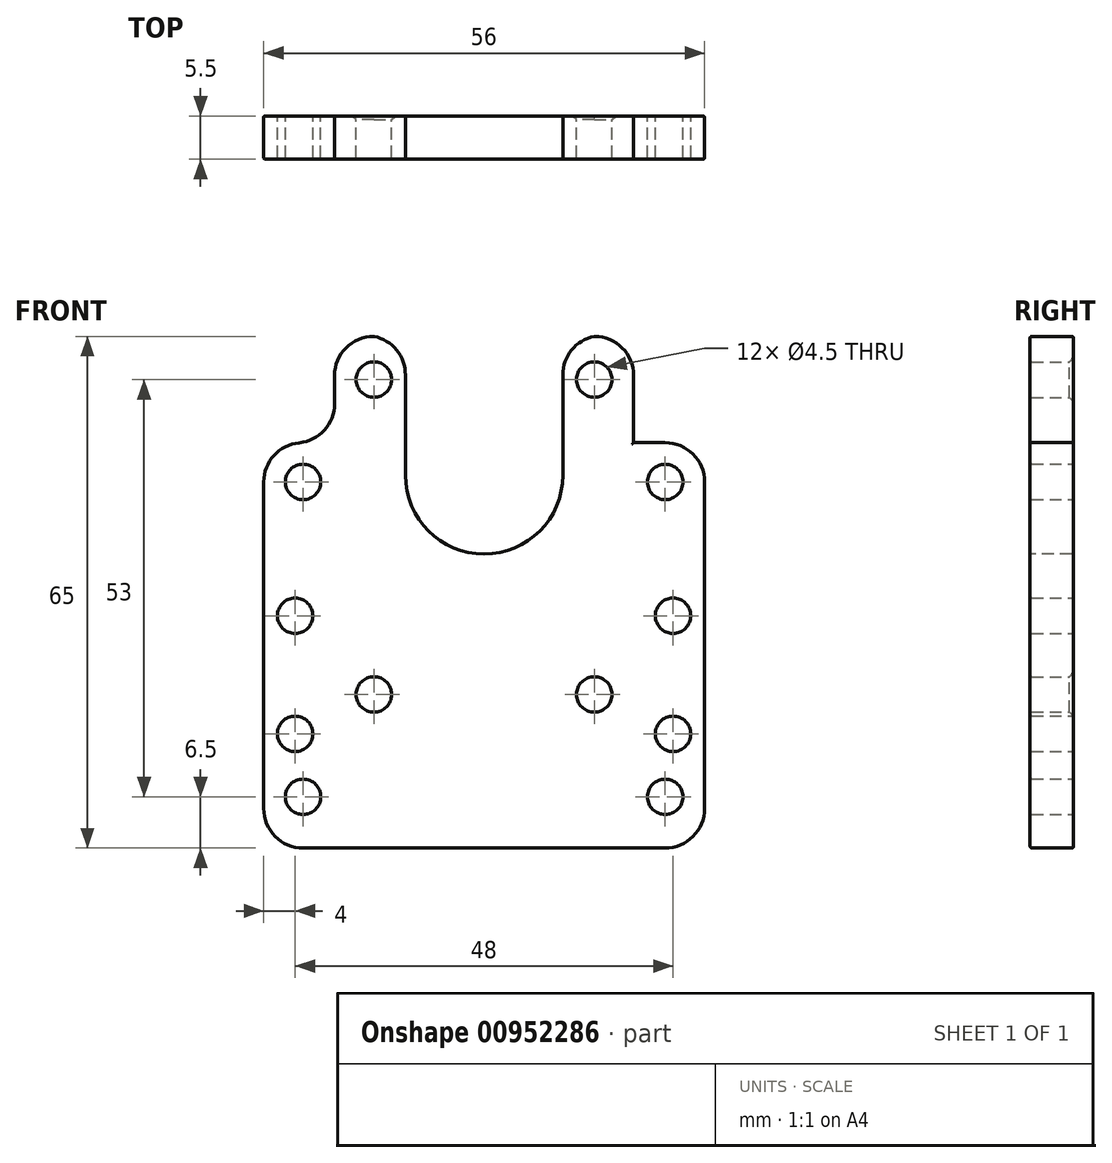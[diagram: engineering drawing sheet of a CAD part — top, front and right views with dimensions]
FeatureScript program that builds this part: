
annotation { "Feature Type Name" : "Feature", "Feature Type Description" : "" }
export const myFeature = defineFeature(function(context is Context, id is Id, definition is map)
    precondition{}
    {
        {
            var Q0;
            Q0=qCreatedBy(makeId("Front.planeOp"),FACE);
            cPlane(context, id + "F0", {"entities" : qUnion([Q0]), "cplaneType" : CPlaneType.OFFSET, "offset" : 13 * mm, "width" : 150 * mm, "height" : 150 * mm});
        }
        {
            var Q0;
            Q0=qCreatedBy(id+"F0.planeOp",FACE);
            var sketch = newSketch(context, id + "F1", { "sketchPlane" : qUnion([Q0])});
            skLineSegment(sketch, "E0.bottom", {"start": v(12, 56.5) * mm, "end": v(50, 56.5) * mm});
            skLineSegment(sketch, "E0.left", {"start": v(12, 56.5) * mm, "end": v(12, -8.5) * mm});
            skLineSegment(sketch, "E0.right", {"start": v(50, 56.5) * mm, "end": v(50, -8.5) * mm});
            skLineSegment(sketch, "E1", {"start": v(31, 77.62) * mm, "end": v(31, -1.76) * mm, "construction": true});
            skLineSegment(sketch, "E2", {"start": v(-19.07, 31) * mm, "end": v(89.66, 31) * mm, "construction": true});
            skCircle(sketch, "E3", {"center": v(45, 51) * mm, "radius": 2.25 * mm});
            skCircle(sketch, "E4", {"center": v(45, 11) * mm, "radius": 2.25 * mm});
            skCircle(sketch, "E5", {"center": v(17, 11) * mm, "radius": 2.25 * mm});
            skCircle(sketch, "E6", {"center": v(17, 51) * mm, "radius": 2.25 * mm});
            skCircle(sketch, "E7", {"center": v(17, 11) * mm, "radius": 3.5 * mm, "construction": true});
            skCircle(sketch, "E8", {"center": v(45, 11) * mm, "radius": 3.5 * mm, "construction": true});
            skCircle(sketch, "E9", {"center": v(17, 51) * mm, "radius": 3.5 * mm, "construction": true});
            skCircle(sketch, "E10", {"center": v(45, 51) * mm, "radius": 3.5 * mm, "construction": true});
            skLineSegment(sketch, "E11", {"start": v(37.5, 20.8) * mm, "end": v(37.5, 18.3) * mm, "construction": true});
            skCircle(sketch, "E12", {"center": v(24.5, 19.55) * mm, "radius": 1.25 * mm});
            skLineSegment(sketch, "E13", {"start": v(38.75, 19.55) * mm, "end": v(36.25, 19.55) * mm, "construction": true});
            skCircle(sketch, "E14", {"center": v(37.5, 19.55) * mm, "radius": 1.25 * mm});
            skCircle(sketch, "E15", {"center": v(7, 6) * mm, "radius": 2.25 * mm});
            skCircle(sketch, "E16.MirrorC", {"center": v(7, 21) * mm, "radius": 2.25 * mm});
            skLineSegment(sketch, "E17.top", {"start": v(50, -8.5) * mm, "end": v(12, -8.5) * mm});
            skArc(sketch, "E18.MirrorCS", {"start": v(8, -8.5) * mm, "mid": v(4.46, -7.04) * mm, "end": v(3, -3.5) * mm});
            skLineSegment(sketch, "E19", {"start": v(8, -8.5) * mm, "end": v(12, -8.5) * mm});
            skPoint(sketch, "E20.MirrorCS.center.orphan", {"position": v(7, 31) * mm});
            skLineSegment(sketch, "E21", {"start": v(3, 38) * mm, "end": v(3, -3.5) * mm});
            skCircle(sketch, "E22", {"center": v(8, -2) * mm, "radius": 2.25 * mm});
            skCircle(sketch, "E23", {"center": v(8, 38) * mm, "radius": 2.25 * mm});
            skArc(sketch, "E24", {"start": v(8, 43) * mm, "mid": v(4.46, 41.54) * mm, "end": v(3, 38) * mm});
            skLineSegment(sketch, "E25", {"start": v(8, 43) * mm, "end": v(12, 43) * mm});
            skSolve(sketch);
        }
        {
            var Q0;
            {var subQ1=sQuery(id+"F1.wireOp",EDGE,"E0.bottom");Q0=makeQuery(id+"F1.imprint","IMPRINT",FACE,{"disambiguationData":[TD([[makeQuery(id+"F1.imprint","IMPRINT",EDGE,{"derivedFrom":subQ1}),-1.0]])]});}
            var Q1;
            {var subQ0=sQuery(id+"F1.wireOp",EDGE,"4c5f126c-7228-4284-9c72-7ca8e39765180.MirrorCS");Q1=makeQuery(id+"F1.imprint","IMPRINT",FACE,{"disambiguationData":[TD([[makeQuery(id+"F1.imprint","IMPRINT",EDGE,{"derivedFrom":subQ0}),1.0]])]});}
            var Q2;
            {var subQ0=sQuery(id+"F1.wireOp",EDGE,"bd2f8090-7cf7-4306-adcd-41070bc121290.MirrorCS");Q2=makeQuery(id+"F1.imprint","IMPRINT",FACE,{"disambiguationData":[TD([[makeQuery(id+"F1.imprint","IMPRINT",EDGE,{"derivedFrom":subQ0}),1.0]])]});}
            var Q3;
            {var subQ0=sQuery(id+"F1.wireOp",EDGE,"4c5f126c-7228-4284-9c72-7ca8e39765180.MirrorCS");Q3=makeQuery(id+"F1.imprint","IMPRINT",FACE,{"disambiguationData":[TD([[makeQuery(id+"F1.imprint","IMPRINT",EDGE,{"derivedFrom":subQ0}),-1.0]])]});}
            var Q4;
            {var subQ0=sQuery(id+"F1.wireOp",EDGE,"E20.MirrorCS");var subQ1=makeQuery(id+"F1.imprint","INTERSECT",VERTEX,{"derivedFrom":[sQuery(id+"F1.wireOp",EDGE,"4c5f126c-7228-4284-9c72-7ca8e39765180.MirrorCS"),subQ0]});Q4=makeQuery(id+"F1.imprint","IMPRINT",FACE,{"disambiguationData":[TD([[makeQuery(id+"F1.imprint","IMPRINT",EDGE,{"disambiguationData":[TD([[subQ1,1.0]])],"derivedFrom":subQ0}),-1.0]])]});}
            var Q5;
            {var subQ0=sQuery(id+"F1.wireOp",EDGE,"28a49bcd-20f1-45de-a4e1-923c5660a67d0.MirrorCS");Q5=makeQuery(id+"F1.imprint","IMPRINT",FACE,{"disambiguationData":[TD([[makeQuery(id+"F1.imprint","IMPRINT",EDGE,{"derivedFrom":subQ0}),-1.0]])]});}
            var Q6;
            {var subQ0=sQuery(id+"F1.wireOp",EDGE,"14a62f3c-94eb-4a37-8f73-e40623ff29c70.MirrorCS");var subQ3=sQuery(id+"F1.wireOp",EDGE,"E20.MirrorCS");var subQ5=makeQuery(id+"F1.imprint","INTERSECT",VERTEX,{"disambiguationData":[OD(1.0)],"derivedFrom":[subQ3,subQ0]});Q6=makeQuery(id+"F1.imprint","IMPRINT",FACE,{"disambiguationData":[TD([[makeQuery(id+"F1.imprint","IMPRINT",EDGE,{"disambiguationData":[TD([[subQ5,1.0]])],"derivedFrom":subQ3}),1.0]])]});}
            var Q7;
            {var subQ0=sQuery(id+"F1.wireOp",EDGE,"c9f7c960-82de-4ad7-af7f-67adeb7fb3330.MirrorCS");Q7=makeQuery(id+"F1.imprint","IMPRINT",FACE,{"disambiguationData":[TD([[makeQuery(id+"F1.imprint","IMPRINT",EDGE,{"derivedFrom":subQ0}),1.0]])]});}
            var Q8;
            {var subQ3=sQuery(id+"F1.wireOp",EDGE,"540323be-f487-4806-8fb1-764a1782e5200.MirrorCS");Q8=makeQuery(id+"F1.imprint","IMPRINT",FACE,{"disambiguationData":[TD([[makeQuery(id+"F1.imprint","IMPRINT",EDGE,{"derivedFrom":subQ3}),-1.0]])]});}
            var Q9;
            {var subQ0=sQuery(id+"F1.wireOp",EDGE,"E20.MirrorCS");var subQ3=sQuery(id+"F1.wireOp",EDGE,"81622e4d-bb80-4ace-9f8c-d33d0fcbef830.MirrorCS");var subQ5=makeQuery(id+"F1.imprint","INTERSECT",VERTEX,{"disambiguationData":[OD(1.0)],"derivedFrom":[subQ0,subQ3]});Q9=makeQuery(id+"F1.imprint","IMPRINT",FACE,{"disambiguationData":[TD([[makeQuery(id+"F1.imprint","IMPRINT",EDGE,{"disambiguationData":[TD([[subQ5,-1.0]])],"derivedFrom":subQ0}),1.0]])]});}
            var Q10;
            {var subQ0=sQuery(id+"F1.wireOp",EDGE,"E20.MirrorCS");var subQ1=makeQuery(id+"F1.imprint","INTERSECT",VERTEX,{"derivedFrom":[subQ0,sQuery(id+"F1.wireOp",EDGE,"c9f7c960-82de-4ad7-af7f-67adeb7fb3330.MirrorCS")]});Q10=makeQuery(id+"F1.imprint","IMPRINT",FACE,{"disambiguationData":[TD([[makeQuery(id+"F1.imprint","IMPRINT",EDGE,{"disambiguationData":[TD([[subQ1,1.0]])],"derivedFrom":subQ0}),-1.0]])]});}
            var Q11;
            {var subQ0=sQuery(id+"F1.wireOp",EDGE,"c9f7c960-82de-4ad7-af7f-67adeb7fb3330.MirrorCS");Q11=makeQuery(id+"F1.imprint","IMPRINT",FACE,{"disambiguationData":[TD([[makeQuery(id+"F1.imprint","IMPRINT",EDGE,{"derivedFrom":subQ0}),-1.0]])]});}
            var Q12;
            {var subQ0=sQuery(id+"F1.wireOp",EDGE,"2b5f1761-41bf-4c5f-a052-8d6cd96bd7f80.MirrorCS");Q12=makeQuery(id+"F1.imprint","IMPRINT",FACE,{"disambiguationData":[TD([[makeQuery(id+"F1.imprint","IMPRINT",EDGE,{"derivedFrom":subQ0}),1.0]])]});}
            var Q13;
            Q13=makeQuery(id+"F1.imprint","IMPRINT",FACE,{"disambiguationData":[TD([[makeQuery(id+"F1.imprint","IMPRINT",EDGE,{"derivedFrom":sQuery(id+"F1.wireOp",EDGE,"044e4ed2-c594-4609-a6b1-d96679fc13440.MirrorC")}),1.0]])]});
            var Q14;
            {var subQ0=sQuery(id+"F1.wireOp",EDGE,"YvGRB0oB-o1B7-2Eru-9MpJ-MU3ItPoMbeSP");var subQ1=sQuery(id+"F1.wireOp",EDGE,"E20.MirrorCS");var subQ2=makeQuery(id+"F1.imprint","INTERSECT",VERTEX,{"derivedFrom":[subQ1,subQ0]});Q14=makeQuery(id+"F1.imprint","IMPRINT",FACE,{"disambiguationData":[TD([[makeQuery(id+"F1.imprint","IMPRINT",EDGE,{"disambiguationData":[TD([[subQ2,-1.0]])],"derivedFrom":subQ1}),1.0]])]});}
            var Q15;
            {var subQ0=sQuery(id+"F1.wireOp",EDGE,"YvGRB0oB-o1B7-2Eru-9MpJ-MU3ItPoMbeSP");var subQ1=sQuery(id+"F1.wireOp",EDGE,"E20.MirrorCS");var subQ2=makeQuery(id+"F1.imprint","INTERSECT",VERTEX,{"derivedFrom":[subQ1,subQ0]});Q15=makeQuery(id+"F1.imprint","IMPRINT",FACE,{"disambiguationData":[TD([[makeQuery(id+"F1.imprint","IMPRINT",EDGE,{"disambiguationData":[TD([[subQ2,1.0]])],"derivedFrom":subQ1}),1.0]])]});}
            var Q16;
            Q16=makeQuery(id+"F1.imprint","IMPRINT",FACE,{"disambiguationData":[TD([[makeQuery(id+"F1.imprint","IMPRINT",EDGE,{"derivedFrom":sQuery(id+"F1.wireOp",EDGE,"044e4ed2-c594-4609-a6b1-d96679fc13440.MirrorC")}),-1.0]])]});
            var Q17;
            {var subQ0=sQuery(id+"F1.wireOp",EDGE,"14a62f3c-94eb-4a37-8f73-e40623ff29c70.MirrorCS");var subQ3=sQuery(id+"F1.wireOp",EDGE,"E20.MirrorCS");var subQ5=makeQuery(id+"F1.imprint","INTERSECT",VERTEX,{"disambiguationData":[OD(0.0)],"derivedFrom":[subQ3,subQ0]});Q17=makeQuery(id+"F1.imprint","IMPRINT",FACE,{"disambiguationData":[TD([[makeQuery(id+"F1.imprint","IMPRINT",EDGE,{"disambiguationData":[TD([[subQ5,1.0]])],"derivedFrom":subQ3}),1.0]])]});}
            var Q18;
            {var subQ1=sQuery(id+"F1.wireOp",EDGE,"81NgzbPt-EB3h-myks-LzxL-Qv06gequt6FA");Q18=makeQuery(id+"F1.imprint","IMPRINT",FACE,{"disambiguationData":[TD([[makeQuery(id+"F1.imprint","IMPRINT",EDGE,{"derivedFrom":subQ1}),1.0]])]});}
            var Q19;
            Q19=makeQuery(id+"F1.imprint","IMPRINT",FACE,{"disambiguationData":[TD([[makeQuery(id+"F1.imprint","IMPRINT",EDGE,{"derivedFrom":sQuery(id+"F1.wireOp",EDGE,"E15")}),-1.0]])]});
            var Q20;
            {var subQ3=sQuery(id+"F1.wireOp",EDGE,"81NgzbPt-EB3h-myks-LzxL-Qv06gequt6FA");Q20=makeQuery(id+"F1.imprint","IMPRINT",FACE,{"disambiguationData":[TD([[makeQuery(id+"F1.imprint","IMPRINT",EDGE,{"derivedFrom":subQ3}),-1.0]])]});}
            var Q21;
            {var subQ3=sQuery(id+"F1.wireOp",EDGE,"ZM5MgDSH-fxbz-2lXx-OnJi-46qlj0q2sVRy");Q21=makeQuery(id+"F1.imprint","IMPRINT",FACE,{"disambiguationData":[TD([[makeQuery(id+"F1.imprint","IMPRINT",EDGE,{"derivedFrom":subQ3}),1.0]])]});}
            var Q22;
            {var subQ0=sQuery(id+"F1.wireOp",EDGE,"ZM5MgDSH-fxbz-2lXx-OnJi-46qlj0q2sVRy");Q22=makeQuery(id+"F1.imprint","IMPRINT",FACE,{"disambiguationData":[TD([[makeQuery(id+"F1.imprint","IMPRINT",EDGE,{"derivedFrom":subQ0}),-1.0]])]});}
            var Q23;
            Q23=makeQuery(id+"F1.imprint","IMPRINT",FACE,{"disambiguationData":[TD([[makeQuery(id+"F1.imprint","IMPRINT",EDGE,{"derivedFrom":sQuery(id+"F1.wireOp",EDGE,"0455397c-a53a-48e8-8fdc-598eec077b450.MirrorC")}),1.0]])]});
            var Q24;
            {var subQ1=sQuery(id+"F1.wireOp",EDGE,"E17.bottom");Q24=makeQuery(id+"F1.imprint","IMPRINT",FACE,{"disambiguationData":[TD([[makeQuery(id+"F1.imprint","IMPRINT",EDGE,{"derivedFrom":subQ1}),1.0]])]});}
            var Q25;
            {var subQ0=sQuery(id+"F1.wireOp",EDGE,"E19");Q25=makeQuery(id+"F1.imprint","IMPRINT",FACE,{"disambiguationData":[TD([[makeQuery(id+"F1.imprint","IMPRINT",EDGE,{"derivedFrom":subQ0}),1.0]])]});}
            var Q26;
            {var subQ5=sQuery(id+"F1.wireOp",EDGE,"ASwXeTtA-wzrH-nalq-PQ0O-iZlBfhMEutyM.bottom");Q26=makeQuery(id+"F1.imprint","IMPRINT",FACE,{"disambiguationData":[TD([[makeQuery(id+"F1.imprint","IMPRINT",EDGE,{"derivedFrom":subQ5}),-1.0]])]});}
            var Q27;
            {var subQ0=sQuery(id+"F1.wireOp",EDGE,"E18.MirrorCS");var subQ1=sQuery(id+"F1.wireOp",EDGE,"E17.right");var subQ2=makeQuery(id+"F1.imprint","INTERSECT",VERTEX,{"disambiguationData":[OD(0.0)],"derivedFrom":[subQ1,subQ0]});Q27=makeQuery(id+"F1.imprint","IMPRINT",FACE,{"disambiguationData":[TD([[makeQuery(id+"F1.imprint","IMPRINT",EDGE,{"disambiguationData":[TD([[subQ2,1.0]])],"derivedFrom":subQ1}),1.0]])]});}
            var Q28;
            Q28=makeQuery(id+"F1.imprint","IMPRINT",FACE,{"disambiguationData":[TD([[makeQuery(id+"F1.imprint","IMPRINT",EDGE,{"derivedFrom":sQuery(id+"F1.wireOp",EDGE,"E12")}),1.0]])]});
            var Q29;
            Q29=makeQuery(id+"F1.imprint","IMPRINT",FACE,{"disambiguationData":[TD([[makeQuery(id+"F1.imprint","IMPRINT",EDGE,{"derivedFrom":sQuery(id+"F1.wireOp",EDGE,"E14")}),1.0]])]});
            extrude(context, id + "F2", {"entities" : qUnion([Q0, Q1, Q2, Q3, Q4, Q5, Q6, Q7, Q8, Q9, Q10, Q11, Q12, Q13, Q14, Q15, Q16, Q17, Q18, Q19, Q20, Q21, Q22, Q23, Q24, Q25, Q26, Q27, Q28, Q29]), "depth" : (4.5 + 1) * mm, "offsetDistance" : 25 * mm});
        }
        {
            var Q0;
            Q0=qCreatedBy(makeId("Front.planeOp"),FACE);
            cPlane(context, id + "F3", {"entities" : qUnion([Q0]), "cplaneType" : CPlaneType.OFFSET, "offset" : 13 * mm, "width" : 150 * mm, "height" : 150 * mm});
        }
        {
            var Q0;
            Q0=qCreatedBy(id+"F3.planeOp",FACE);
            var sketch = newSketch(context, id + "F4", { "sketchPlane" : qUnion([Q0])});
            skLineSegment(sketch, "E26.bottom", {"start": v(26, 70.22) * mm, "end": v(36, 70.22) * mm});
            skLineSegment(sketch, "E26.top", {"start": v(26, 32.5) * mm, "end": v(36, 32.5) * mm});
            skLineSegment(sketch, "E26.left", {"start": v(26, 70.22) * mm, "end": v(26, 32.5) * mm});
            skLineSegment(sketch, "E26.right", {"start": v(36, 70.22) * mm, "end": v(36, 32.5) * mm});
            skLineSegment(sketch, "E27", {"start": v(31, 83.23) * mm, "end": v(31, -17.57) * mm, "construction": true});
            skSolve(sketch);
        }
        {
            var Q0;
            Q0 = qSketchRegion(id + "F4", true);
            extrude(context, id + "F5", {"entities" : qUnion([Q0]), "operationType" : NewBodyOperationType.REMOVE, "endBound" : BoundingType.THROUGH_ALL, "oppositeDirection" : true, "depth" : 25 * mm, "offsetDistance" : 25 * mm});
        }
        {
            var Q0;
            Q0=qCreatedBy(makeId("Front.planeOp"),FACE);
            var Q1;
            Q1 = qBodyType(qCreatedBy(id + "F7" ,EDGE), BodyType.WIRE);
            cPlane(context, id + "F6", {"entities" : qUnion([Q0, Q1]), "cplaneType" : CPlaneType.OFFSET, "offset" : 13 * mm, "width" : 150 * mm, "height" : 150 * mm});
        }
        {
            var Q0;
            Q0=qCreatedBy(id+"F6.planeOp",FACE);
            var sketch = newSketch(context, id + "F7", { "sketchPlane" : qUnion([Q0])});
            skCircle(sketch, "E28", {"center": v(17, 21) * mm, "radius": 2.25 * mm});
            skCircle(sketch, "E29", {"center": v(45, 21) * mm, "radius": 2.25 * mm});
            skSolve(sketch);
        }
        {
            var Q0;
            Q0 = qSketchRegion(id + "F7", true);
            extrude(context, id + "F8", {"entities" : qUnion([Q0]), "operationType" : NewBodyOperationType.REMOVE, "endBound" : BoundingType.THROUGH_ALL, "oppositeDirection" : true, "depth" : 25 * mm, "offsetDistance" : 25 * mm});
        }
        {
            var Q0;
            Q0=qCreatedBy(makeId("Front.planeOp"),FACE);
            cPlane(context, id + "F9", {"entities" : qUnion([Q0]), "cplaneType" : CPlaneType.OFFSET, "offset" : 10 * mm, "width" : 150 * mm, "height" : 150 * mm});
        }
        {
            var Q0;
            Q0=qCreatedBy(id+"F9.planeOp",FACE);
            var sketch = newSketch(context, id + "F10", { "sketchPlane" : qUnion([Q0])});
            skArc(sketch, "E30", {"start": v(17, 16) * mm, "mid": v(22, 21) * mm, "end": v(17, 26) * mm});
            skArc(sketch, "E31", {"start": v(45, 26) * mm, "mid": v(40, 21) * mm, "end": v(45, 16) * mm});
            skLineSegment(sketch, "E32", {"start": v(17, 26) * mm, "end": v(3.21, 26) * mm});
            skLineSegment(sketch, "E33", {"start": v(3.21, 26) * mm, "end": v(3.21, 16) * mm});
            skLineSegment(sketch, "E34", {"start": v(3.21, 16) * mm, "end": v(17, 16) * mm});
            skLineSegment(sketch, "E35", {"start": v(45, 26) * mm, "end": v(58.79, 26) * mm});
            skLineSegment(sketch, "E36", {"start": v(58.79, 26) * mm, "end": v(58.79, 16) * mm});
            skLineSegment(sketch, "E37", {"start": v(58.79, 16) * mm, "end": v(45, 16) * mm});
            skSolve(sketch);
        }
        {
            var Q0;
            Q0 = qSketchRegion(id + "F10", true);
            var Q1;
            Q1 = qSketchRegion(id + "F10", true);
            extrude(context, id + "F11", {"entities" : qUnion([Q0, Q1]), "operationType" : NewBodyOperationType.REMOVE, "endBound" : BoundingType.THROUGH_ALL, "oppositeDirection" : true, "depth" : 25 * mm, "offsetDistance" : 25 * mm});
        }
        {
            var Q0;
            Q0=makeQuery(id+"F2.opExtrude","CAP_FACE",FACE,{"disambiguationData":[OSD([sQuery(id+"F1.wireOp",EDGE,"E0.bottom"),sQuery(id+"F1.wireOp",EDGE,"E0.top"),sQuery(id+"F1.wireOp",EDGE,"E0.left"),sQuery(id+"F1.wireOp",EDGE,"E0.right"),sQuery(id+"F1.wireOp",EDGE,"E3"),sQuery(id+"F1.wireOp",EDGE,"E4"),sQuery(id+"F1.wireOp",EDGE,"E5"),sQuery(id+"F1.wireOp",EDGE,"E6"),sQuery(id+"F1.wireOp",EDGE,"E12"),sQuery(id+"F1.wireOp",EDGE,"E14")])],"isStart":false});
            cPlane(context, id + "F12", {"entities" : qUnion([Q0]), "cplaneType" : CPlaneType.OFFSET, "offset" : (1.5 + 1) * mm, "oppositeDirection" : true, "width" : 150 * mm, "height" : 150 * mm});
        }
        {
            var Q0;
            Q0=qCreatedBy(id+"F12.planeOp",FACE);
            var sketch = newSketch(context, id + "F13", { "sketchPlane" : qUnion([Q0])});
            skLineSegment(sketch, "E38.bottom", {"start": v(22, 37.94) * mm, "end": v(40, 37.94) * mm});
            skLineSegment(sketch, "E38.top", {"start": v(22, 28.85) * mm, "end": v(40, 28.85) * mm});
            skLineSegment(sketch, "E38.left", {"start": v(40, 28.85) * mm, "end": v(40, 37.94) * mm});
            skLineSegment(sketch, "E38.right", {"start": v(22, 28.85) * mm, "end": v(22, 37.94) * mm});
            skLineSegment(sketch, "E39", {"start": v(31, 70.54) * mm, "end": v(31, 32.5) * mm, "construction": true});
            skSolve(sketch);
        }
        {
            var Q0;
            Q0 = qSketchRegion(id + "F13", true);
            extrude(context, id + "F14", {"entities" : qUnion([Q0]), "operationType" : NewBodyOperationType.REMOVE, "endBound" : BoundingType.THROUGH_ALL, "depth" : 25 * mm, "offsetDistance" : 25 * mm});
        }
        {
            var Q0;
            Q0=qCreatedBy(makeId("Front.planeOp"),FACE);
            cPlane(context, id + "F15", {"entities" : qUnion([Q0]), "cplaneType" : CPlaneType.OFFSET, "offset" : ((13 - 0.3 - 1.5 - 1.2) - 2.5) * mm, "width" : 150 * mm, "height" : 150 * mm});
        }
        {
            var Q0;
            Q0=qCreatedBy(id+"F15.planeOp",FACE);
            var sketch = newSketch(context, id + "F16", { "sketchPlane" : qUnion([Q0])});
            skLineSegment(sketch, "E40.bottom", {"start": v(21, 63.4) * mm, "end": v(41, 63.4) * mm});
            skLineSegment(sketch, "E40.left", {"start": v(21, 63.4) * mm, "end": v(21, 28.85) * mm});
            skLineSegment(sketch, "E40.right", {"start": v(41, 63.4) * mm, "end": v(41, 28.85) * mm});
            skLineSegment(sketch, "E41", {"start": v(41, 28.85) * mm, "end": v(21, 28.85) * mm});
            skPoint(sketch, "E42", {"position": v(31, 28.85) * mm});
            skSolve(sketch);
        }
        {
            var Q0;
            Q0 = qSketchRegion(id + "F16", true);
            extrude(context, id + "F17", {"entities" : qUnion([Q0]), "operationType" : NewBodyOperationType.REMOVE, "endBound" : BoundingType.THROUGH_ALL, "depth" : 25 * mm, "offsetDistance" : 25 * mm});
        }
        {
            var Q0;
            Q0=qCreatedBy(makeId("Right.planeOp"),FACE);
            cPlane(context, id + "F18", {"entities" : qUnion([Q0]), "cplaneType" : CPlaneType.OFFSET, "offset" : 31 * mm, "width" : 150 * mm, "height" : 150 * mm});
        }
        {
            var Q0;
            Q0=makeQuery(id+"F2.opExtrude","SWEPT_BODY",BODY,{"disambiguationData":[OSD([sQuery(id+"F1.wireOp",EDGE,"E0.bottom"),sQuery(id+"F1.wireOp",EDGE,"E0.left"),sQuery(id+"F1.wireOp",EDGE,"E0.right"),sQuery(id+"F1.wireOp",EDGE,"E3"),sQuery(id+"F1.wireOp",EDGE,"E4"),sQuery(id+"F1.wireOp",EDGE,"E5"),sQuery(id+"F1.wireOp",EDGE,"E6"),sQuery(id+"F1.wireOp",EDGE,"E12"),sQuery(id+"F1.wireOp",EDGE,"E14"),sQuery(id+"F1.wireOp",EDGE,"IY8wMdms-gyv0-al8N-HDtY-5mPgr8BnwYFw"),sQuery(id+"F1.wireOp",EDGE,"ZM5MgDSH-fxbz-2lXx-OnJi-46qlj0q2sVRy"),sQuery(id+"F1.wireOp",EDGE,"81NgzbPt-EB3h-myks-LzxL-Qv06gequt6FA"),sQuery(id+"F1.wireOp",EDGE,"E15"),sQuery(id+"F1.wireOp",EDGE,"q3XicaxJ-DnTj-KL0w-2k1l-DKEAq9ySnp1d"),sQuery(id+"F1.wireOp",EDGE,"4c5f126c-7228-4284-9c72-7ca8e39765180.MirrorCS"),sQuery(id+"F1.wireOp",EDGE,"E20.MirrorCS"),sQuery(id+"F1.wireOp",EDGE,"044e4ed2-c594-4609-a6b1-d96679fc13440.MirrorC"),sQuery(id+"F1.wireOp",EDGE,"c9f7c960-82de-4ad7-af7f-67adeb7fb3330.MirrorCS")])]});
            var Q1;
            Q1=qCreatedBy(id+"F18.planeOp",FACE);
            mirror(context, id + "F19", {"operationType" : NewBodyOperationType.ADD, "entities" : qUnion([Q0]), "mirrorPlane" : qUnion([Q1])});
        }
        {
            var Q0;
            Q0=makeQuery(id+"F11.boolean.opBoolean","INTERSECT",EDGE,{"derivedFrom":[makeQuery(id+"F8.boolean.opBoolean","COPY",FACE,{"derivedFrom":makeQuery(id+"F8.opExtrude","SWEPT_FACE",FACE,{"disambiguationData":[OSD([sQuery(id+"F7.wireOp",EDGE,"E29")])]})}),makeQuery(id+"F11.opExtrude","CAP_FACE",FACE,{"disambiguationData":[OSD([sQuery(id+"F10.wireOp",EDGE,"E31"),sQuery(id+"F10.wireOp",EDGE,"E35"),sQuery(id+"F10.wireOp",EDGE,"E36"),sQuery(id+"F10.wireOp",EDGE,"E37")])],"isStart":true})]});
            var Q1;
            Q1=makeQuery(id+"F11.boolean.opBoolean","INTERSECT",EDGE,{"derivedFrom":[makeQuery(id+"F8.boolean.opBoolean","COPY",FACE,{"derivedFrom":makeQuery(id+"F8.opExtrude","SWEPT_FACE",FACE,{"disambiguationData":[OSD([sQuery(id+"F7.wireOp",EDGE,"E28")])]})}),makeQuery(id+"F11.opExtrude","CAP_FACE",FACE,{"disambiguationData":[OSD([sQuery(id+"F10.wireOp",EDGE,"E30"),sQuery(id+"F10.wireOp",EDGE,"E32"),sQuery(id+"F10.wireOp",EDGE,"E33"),sQuery(id+"F10.wireOp",EDGE,"E34")])],"isStart":true})]});
            var Q2;
            Q2=makeQuery(id+"F2.opExtrude","CAP_EDGE",EDGE,{"disambiguationData":[OSD([sQuery(id+"F1.wireOp",EDGE,"E6")])],"isStart":true});
            var Q3;
            Q3=makeQuery(id+"F2.opExtrude","CAP_EDGE",EDGE,{"disambiguationData":[OSD([sQuery(id+"F1.wireOp",EDGE,"E3")])],"isStart":true});
            var Q4;
            Q4=makeQuery(id+"F2.opExtrude","CAP_EDGE",EDGE,{"disambiguationData":[OSD([sQuery(id+"F1.wireOp",EDGE,"E4")])],"isStart":true});
            var Q5;
            Q5=makeQuery(id+"F2.opExtrude","CAP_EDGE",EDGE,{"disambiguationData":[OSD([sQuery(id+"F1.wireOp",EDGE,"E5")])],"isStart":true});
            chamfer(context, id + "F20", {"entities" : qUnion([Q0, Q1, Q2, Q3, Q4, Q5]), "width" : 0.5 * mm, "tangentPropagation" : true});
        }
        {
            var Q0;
            Q0=makeQuery(id+"F2.opExtrude","SWEPT_EDGE",EDGE,{"disambiguationData":[OSD([sQuery(id+"F1.wireOp",EDGE,"E0.bottom"),sQuery(id+"F1.wireOp",EDGE,"E0.left")])]});
            var Q1;
            Q1=makeQuery(id+"F2.opExtrude","SWEPT_EDGE",EDGE,{"disambiguationData":[OSD([sQuery(id+"F1.wireOp",EDGE,"E0.top"),sQuery(id+"F1.wireOp",EDGE,"E0.left")])]});
            var Q2;
            Q2=makeQuery(id+"F2.opExtrude","SWEPT_EDGE",EDGE,{"disambiguationData":[OSD([sQuery(id+"F1.wireOp",EDGE,"E0.top"),sQuery(id+"F1.wireOp",EDGE,"E0.right")])]});
            var Q3;
            Q3=makeQuery(id+"F2.opExtrude","SWEPT_EDGE",EDGE,{"disambiguationData":[OSD([sQuery(id+"F1.wireOp",EDGE,"E0.bottom"),sQuery(id+"F1.wireOp",EDGE,"E0.right")])]});
            var Q4;
            Q4=makeQuery(id+"F19.opPattern","COPY",EDGE,{"derivedFrom":makeQuery(id+"F2.opExtrude","SWEPT_EDGE",EDGE,{"disambiguationData":[OSD([sQuery(id+"F1.wireOp",EDGE,"E0.left"),sQuery(id+"F1.wireOp",EDGE,"c9f7c960-82de-4ad7-af7f-67adeb7fb3330.MirrorCS")])]}),"instanceName":"1"});
            var Q5;
            Q5=makeQuery(id+"F19.opPattern","COPY",EDGE,{"derivedFrom":makeQuery(id+"F2.opExtrude","SWEPT_EDGE",EDGE,{"disambiguationData":[OSD([sQuery(id+"F1.wireOp",EDGE,"E0.left"),sQuery(id+"F1.wireOp",EDGE,"4c5f126c-7228-4284-9c72-7ca8e39765180.MirrorCS")])]}),"instanceName":"1"});
            var Q6;
            Q6=makeQuery(id+"F19.opPattern","COPY",EDGE,{"derivedFrom":makeQuery(id+"F2.opExtrude","SWEPT_EDGE",EDGE,{"disambiguationData":[OSD([sQuery(id+"F1.wireOp",EDGE,"E0.left"),sQuery(id+"F1.wireOp",EDGE,"81NgzbPt-EB3h-myks-LzxL-Qv06gequt6FA")])]}),"instanceName":"1"});
            var Q7;
            Q7=makeQuery(id+"F2.opExtrude","SWEPT_EDGE",EDGE,{"disambiguationData":[OSD([sQuery(id+"F1.wireOp",EDGE,"E0.left"),sQuery(id+"F1.wireOp",EDGE,"ZM5MgDSH-fxbz-2lXx-OnJi-46qlj0q2sVRy"),sQuery(id+"F1.wireOp",EDGE,"q3XicaxJ-DnTj-KL0w-2k1l-DKEAq9ySnp1d")])]});
            fillet(context, id + "F21", {"entities" : qUnion([Q0, Q1, Q2, Q3, Q4, Q5, Q6, Q7]), "radius" : 5 * mm, "tangentPropagation" : true, "defaultsChanged" : false, "vertexSettings" : [], "allowEdgeOverflow" : false});
        }
        {
            var Q0;
            Q0=makeQuery(id+"F17.boolean.opBoolean","COPY",EDGE,{"derivedFrom":makeQuery(id+"F17.opExtrude","SWEPT_EDGE",EDGE,{"disambiguationData":[OSD([sQuery(id+"F16.wireOp",EDGE,"E40.left"),sQuery(id+"F16.wireOp",EDGE,"E41")])]})});
            var Q1;
            Q1=makeQuery(id+"F17.boolean.opBoolean","COPY",EDGE,{"derivedFrom":makeQuery(id+"F17.opExtrude","SWEPT_EDGE",EDGE,{"disambiguationData":[OSD([sQuery(id+"F16.wireOp",EDGE,"E40.right"),sQuery(id+"F16.wireOp",EDGE,"E41")])]})});
            fillet(context, id + "F22", {"entities" : qUnion([Q0, Q1]), "radius" : 10 * mm, "tangentPropagation" : true, "defaultsChanged" : false, "vertexSettings" : [], "allowEdgeOverflow" : false});
        }
        {
            var Q0;
            {var subQ17=sQuery(id+"F1.wireOp",EDGE,"E0.bottom");Q0=makeQuery(id+"F17.boolean.opBoolean","INTERSECT",EDGE,{"derivedFrom":[makeQuery(id+"F5.boolean.opBoolean","SPLIT",FACE,{"disambiguationData":[TD([makeQuery(id+"F5.opExtrude","SWEPT_FACE",FACE,{"disambiguationData":[OSD([sQuery(id+"F4.wireOp",EDGE,"E26.left")])]})])],"derivedFrom":makeQuery(id+"F2.opExtrude","SWEPT_FACE",FACE,{"disambiguationData":[OSD([subQ17])]})}),makeQuery(id+"F17.opExtrude","SWEPT_FACE",FACE,{"disambiguationData":[OSD([sQuery(id+"F16.wireOp",EDGE,"E40.left")])]})]});}
            var Q1;
            {var subQ15=sQuery(id+"F1.wireOp",EDGE,"E0.right");var subQ17=sQuery(id+"F1.wireOp",EDGE,"E0.bottom");Q1=makeQuery(id+"F17.boolean.opBoolean","INTERSECT",EDGE,{"derivedFrom":[makeQuery(id+"F5.boolean.opBoolean","SPLIT",FACE,{"disambiguationData":[TD([makeQuery(id+"F2.opExtrude","SWEPT_FACE",FACE,{"disambiguationData":[OSD([subQ15])]})])],"derivedFrom":makeQuery(id+"F2.opExtrude","SWEPT_FACE",FACE,{"disambiguationData":[OSD([subQ17])]})}),makeQuery(id+"F17.opExtrude","SWEPT_FACE",FACE,{"disambiguationData":[OSD([sQuery(id+"F16.wireOp",EDGE,"E40.right")])]})]});}
            var Q2;
            Q2=makeQuery(id+"F19.opPattern","COPY",EDGE,{"derivedFrom":makeQuery(id+"F2.opExtrude","SWEPT_EDGE",EDGE,{"disambiguationData":[OSD([sQuery(id+"F1.wireOp",EDGE,"E17.bottom"),sQuery(id+"F1.wireOp",EDGE,"ASwXeTtA-wzrH-nalq-PQ0O-iZlBfhMEutyM.bottom"),sQuery(id+"F1.wireOp",EDGE,"ASwXeTtA-wzrH-nalq-PQ0O-iZlBfhMEutyM.right")])]}),"instanceName":"1"});
            var Q3;
            Q3=makeQuery(id+"F19.opPattern","COPY",EDGE,{"derivedFrom":makeQuery(id+"F2.opExtrude","SWEPT_EDGE",EDGE,{"disambiguationData":[OSD([sQuery(id+"F1.wireOp",EDGE,"E17.top"),sQuery(id+"F1.wireOp",EDGE,"ASwXeTtA-wzrH-nalq-PQ0O-iZlBfhMEutyM.right")])]}),"instanceName":"1"});
            var Q4;
            Q4=makeQuery(id+"F2.opExtrude","SWEPT_EDGE",EDGE,{"disambiguationData":[OSD([sQuery(id+"F1.wireOp",EDGE,"E17.bottom"),sQuery(id+"F1.wireOp",EDGE,"ASwXeTtA-wzrH-nalq-PQ0O-iZlBfhMEutyM.bottom"),sQuery(id+"F1.wireOp",EDGE,"ASwXeTtA-wzrH-nalq-PQ0O-iZlBfhMEutyM.right")])]});
            var Q5;
            Q5=makeQuery(id+"F2.opExtrude","SWEPT_EDGE",EDGE,{"disambiguationData":[OSD([sQuery(id+"F1.wireOp",EDGE,"E17.top"),sQuery(id+"F1.wireOp",EDGE,"ASwXeTtA-wzrH-nalq-PQ0O-iZlBfhMEutyM.right")])]});
            fillet(context, id + "F23", {"entities" : qUnion([Q0, Q1, Q2, Q3, Q4, Q5]), "radius" : 5 * mm, "tangentPropagation" : true, "defaultsChanged" : false, "vertexSettings" : [], "allowEdgeOverflow" : false});
        }
        {
            var Q0;
            {var subQ0=makeQuery(id+"F2.opExtrude","CAP_FACE",FACE,{"disambiguationData":[OSD([sQuery(id+"F1.wireOp",EDGE,"E0.bottom"),sQuery(id+"F1.wireOp",EDGE,"E0.left"),sQuery(id+"F1.wireOp",EDGE,"E0.right"),sQuery(id+"F1.wireOp",EDGE,"E3"),sQuery(id+"F1.wireOp",EDGE,"E4"),sQuery(id+"F1.wireOp",EDGE,"E5"),sQuery(id+"F1.wireOp",EDGE,"E6"),sQuery(id+"F1.wireOp",EDGE,"E12"),sQuery(id+"F1.wireOp",EDGE,"E14"),sQuery(id+"F1.wireOp",EDGE,"IY8wMdms-gyv0-al8N-HDtY-5mPgr8BnwYFw"),sQuery(id+"F1.wireOp",EDGE,"ZM5MgDSH-fxbz-2lXx-OnJi-46qlj0q2sVRy"),sQuery(id+"F1.wireOp",EDGE,"81NgzbPt-EB3h-myks-LzxL-Qv06gequt6FA"),sQuery(id+"F1.wireOp",EDGE,"E15"),sQuery(id+"F1.wireOp",EDGE,"q3XicaxJ-DnTj-KL0w-2k1l-DKEAq9ySnp1d"),sQuery(id+"F1.wireOp",EDGE,"4c5f126c-7228-4284-9c72-7ca8e39765180.MirrorCS"),sQuery(id+"F1.wireOp",EDGE,"E20.MirrorCS"),sQuery(id+"F1.wireOp",EDGE,"044e4ed2-c594-4609-a6b1-d96679fc13440.MirrorC"),sQuery(id+"F1.wireOp",EDGE,"c9f7c960-82de-4ad7-af7f-67adeb7fb3330.MirrorCS")])],"isStart":true});Q0=makeQuery(id+"F22.opFillet","BLEND_EDGE",EDGE,{"blendedFrom":[makeQuery(id+"F17.boolean.opBoolean","COPY",EDGE,{"derivedFrom":makeQuery(id+"F17.opExtrude","SWEPT_EDGE",EDGE,{"disambiguationData":[OSD([sQuery(id+"F16.wireOp",EDGE,"E40.left"),sQuery(id+"F16.wireOp",EDGE,"E41")])]})}),makeQuery(id+"F19.boolean.opBoolean","MERGE",FACE,{"derivedFrom":[subQ0,makeQuery(id+"F19.opPattern","COPY",FACE,{"derivedFrom":subQ0,"instanceName":"1"})]})],"blendedInto":[makeQuery(id+"F19.boolean.opBoolean","MERGE",FACE,{"derivedFrom":[subQ0,makeQuery(id+"F19.opPattern","COPY",FACE,{"derivedFrom":subQ0,"instanceName":"1"})]})]});}
            fillet(context, id + "F24", {"entities" : qUnion([Q0]), "tangentPropagation" : true, "radius" : 0.2 * mm, "defaultsChanged" : true, "vertexSettings" : [], "allowEdgeOverflow" : false});
        }
        {
            var Q0;
            {var subQ0=makeQuery(id+"F2.opExtrude","CAP_FACE",FACE,{"disambiguationData":[OSD([sQuery(id+"F1.wireOp",EDGE,"E0.bottom"),sQuery(id+"F1.wireOp",EDGE,"E0.left"),sQuery(id+"F1.wireOp",EDGE,"E0.right"),sQuery(id+"F1.wireOp",EDGE,"E3"),sQuery(id+"F1.wireOp",EDGE,"E4"),sQuery(id+"F1.wireOp",EDGE,"E5"),sQuery(id+"F1.wireOp",EDGE,"E6"),sQuery(id+"F1.wireOp",EDGE,"E15"),sQuery(id+"F1.wireOp",EDGE,"E16.MirrorC"),sQuery(id+"F1.wireOp",EDGE,"E17.top"),sQuery(id+"F1.wireOp",EDGE,"E18.MirrorCS"),sQuery(id+"F1.wireOp",EDGE,"E19"),sQuery(id+"F1.wireOp",EDGE,"E21"),sQuery(id+"F1.wireOp",EDGE,"E22"),sQuery(id+"F1.wireOp",EDGE,"E23"),sQuery(id+"F1.wireOp",EDGE,"E24"),sQuery(id+"F1.wireOp",EDGE,"E25")])],"isStart":true});Q0=makeQuery(id+"F19.boolean.opBoolean","MERGE",FACE,{"derivedFrom":[subQ0,makeQuery(id+"F19.opPattern","COPY",FACE,{"derivedFrom":subQ0,"instanceName":"1"})]});}
            var Q1;
            {var subQ0=makeQuery(id+"F2.opExtrude","CAP_FACE",FACE,{"disambiguationData":[OSD([sQuery(id+"F1.wireOp",EDGE,"E0.bottom"),sQuery(id+"F1.wireOp",EDGE,"E0.left"),sQuery(id+"F1.wireOp",EDGE,"E0.right"),sQuery(id+"F1.wireOp",EDGE,"E3"),sQuery(id+"F1.wireOp",EDGE,"E4"),sQuery(id+"F1.wireOp",EDGE,"E5"),sQuery(id+"F1.wireOp",EDGE,"E6"),sQuery(id+"F1.wireOp",EDGE,"E15"),sQuery(id+"F1.wireOp",EDGE,"E16.MirrorC"),sQuery(id+"F1.wireOp",EDGE,"E17.top"),sQuery(id+"F1.wireOp",EDGE,"E18.MirrorCS"),sQuery(id+"F1.wireOp",EDGE,"E19"),sQuery(id+"F1.wireOp",EDGE,"E21"),sQuery(id+"F1.wireOp",EDGE,"E22"),sQuery(id+"F1.wireOp",EDGE,"E23"),sQuery(id+"F1.wireOp",EDGE,"E24"),sQuery(id+"F1.wireOp",EDGE,"E25")])],"isStart":false});Q1=makeQuery(id+"F19.boolean.opBoolean","MERGE",FACE,{"derivedFrom":[subQ0,makeQuery(id+"F19.opPattern","COPY",FACE,{"derivedFrom":subQ0,"instanceName":"1"})]});}
            fillet(context, id + "F25", {"entities" : qUnion([Q0, Q1]), "tangentPropagation" : true, "radius" : 0.2 * mm, "defaultsChanged" : false, "vertexSettings" : [], "allowEdgeOverflow" : false});
        }
    });
